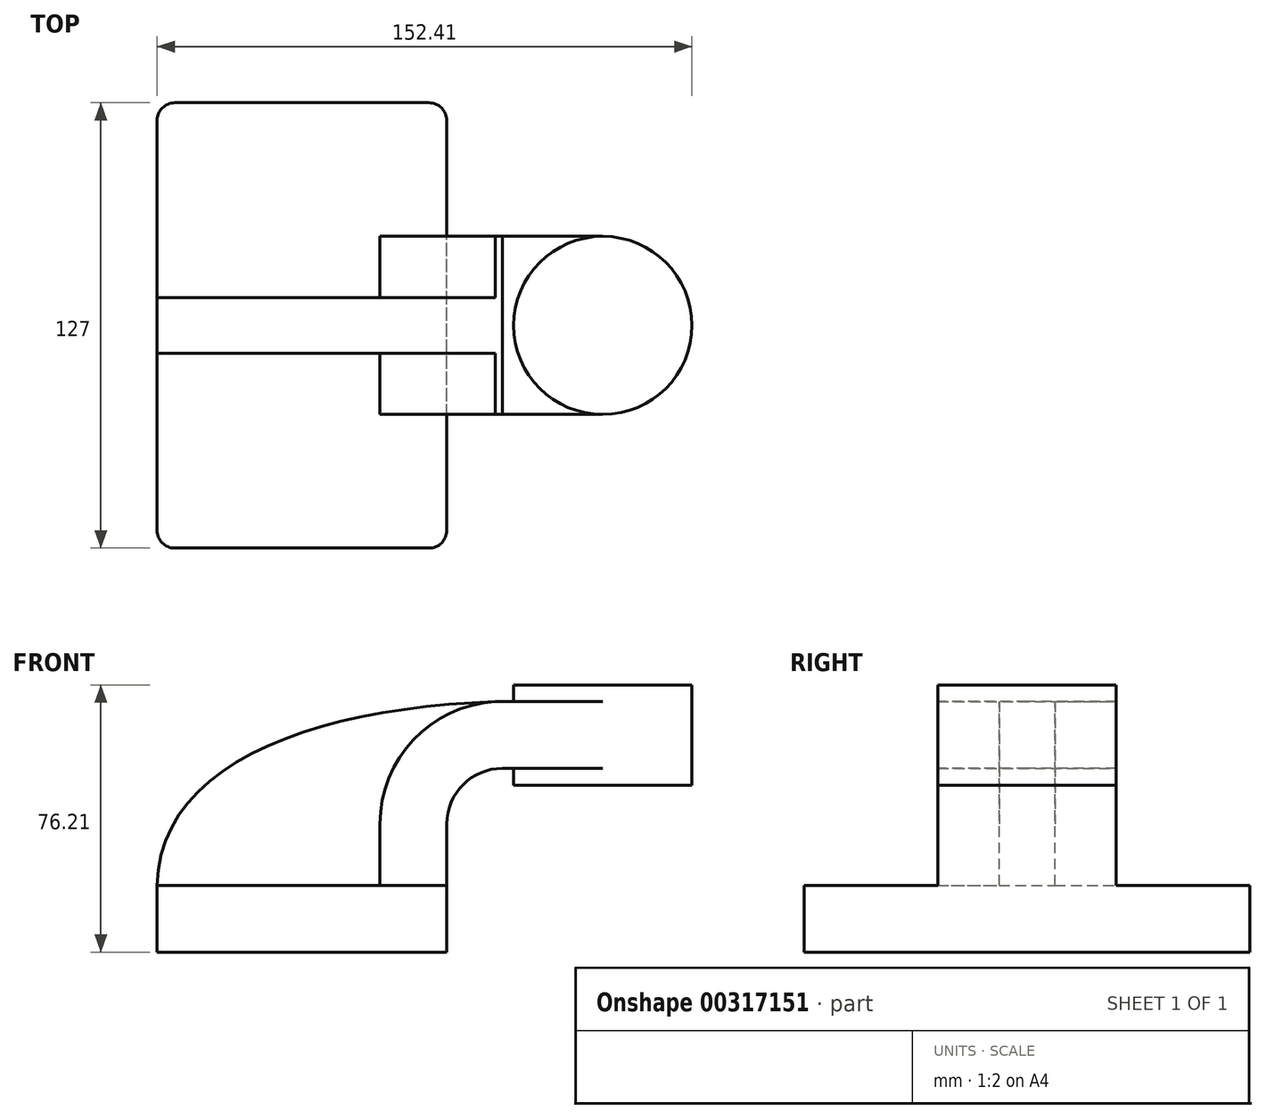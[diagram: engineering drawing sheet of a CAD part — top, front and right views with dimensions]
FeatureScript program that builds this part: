
annotation { "Feature Type Name" : "Feature", "Feature Type Description" : "" }
export const myFeature = defineFeature(function(context is Context, id is Id, definition is map)
    precondition{}
    {
        {
            var Q0;
            Q0=qCreatedBy(makeId("Front.planeOp"),FACE);
            var sketch = newSketch(context, id + "F0", { "sketchPlane" : qUnion([Q0])});
            skLineSegment(sketch, "E0.bottom", {"start": v(-41.28, -9.53) * mm, "end": v(41.28, -9.53) * mm});
            skLineSegment(sketch, "E0.top", {"start": v(-41.28, 9.52) * mm, "end": v(41.28, 9.52) * mm});
            skLineSegment(sketch, "E0.left", {"start": v(-41.28, -9.53) * mm, "end": v(-41.28, 9.52) * mm});
            skLineSegment(sketch, "E0.right", {"start": v(41.28, -9.53) * mm, "end": v(41.28, 9.52) * mm});
            skPoint(sketch, "E0.middle", {"position": v(0, 0) * mm});
            skLineSegment(sketch, "E1.bottom", {"start": v(60.33, 66.68) * mm, "end": v(111.12, 66.68) * mm});
            skLineSegment(sketch, "E1.top", {"start": v(60.33, 38.1) * mm, "end": v(111.12, 38.1) * mm});
            skLineSegment(sketch, "E1.left", {"start": v(60.33, 66.68) * mm, "end": v(60.33, 38.1) * mm});
            skLineSegment(sketch, "E1.right", {"start": v(111.12, 66.68) * mm, "end": v(111.12, 38.1) * mm});
            skPoint(sketch, "E1.middle", {"position": v(85.72, 52.39) * mm});
            skLineSegment(sketch, "E2", {"start": v(41.27, 9.52) * mm, "end": v(41.27, 27) * mm});
            skArc(sketch, "E3", {"start": v(41.27, 27) * mm, "mid": v(45.92, 38.23) * mm, "end": v(57.15, 42.88) * mm});
            skLineSegment(sketch, "E4", {"start": v(57.15, 42.88) * mm, "end": v(85.73, 42.88) * mm});
            skLineSegment(sketch, "E5.0", {"start": v(57.15, 61.93) * mm, "end": v(85.72, 61.93) * mm});
            skArc(sketch, "E5.1", {"start": v(22.22, 27) * mm, "mid": v(32.45, 51.7) * mm, "end": v(57.15, 61.93) * mm});
            skLineSegment(sketch, "E5.2", {"start": v(22.22, 9.52) * mm, "end": v(22.22, 27) * mm});
            skLineSegment(sketch, "E6", {"start": v(85.72, 38.1) * mm, "end": v(85.72, 66.68) * mm});
            skFitSpline(sketch, "E7", {"points": [v(-41.28, 9.53) * mm, v(57.15, 61.93) * mm], "startDerivative": vector(2, 105.97) * mm, "endDerivative": vector(156.9, 3.96) * mm});
            skSolve(sketch);
        }
        {
            var Q0;
            Q0=makeQuery(id+"F0.imprint","IMPRINT",FACE,{"disambiguationData":[TD([[makeQuery(id+"F0.imprint","IMPRINT",EDGE,{"derivedFrom":sQuery(id+"F0.wireOp",EDGE,"E0.bottom")}),1.0]])]});
            extrude(context, id + "F1", {"entities" : qUnion([Q0]), "endBound" : BoundingType.SYMMETRIC, "depth" : 127 * mm});
        }
        {
            var Q0;
            {var subQ1=sQuery(id+"F0.wireOp",EDGE,"E2");Q0=makeQuery(id+"F0.imprint","IMPRINT",FACE,{"disambiguationData":[TD([[makeQuery(id+"F0.imprint","IMPRINT",EDGE,{"derivedFrom":subQ1}),1.0]])]});}
            var Q1;
            {var subQ0=sQuery(id+"F0.wireOp",EDGE,"E5.0");var subQ1=sQuery(id+"F0.wireOp",EDGE,"E1.left");var subQ2=makeQuery(id+"F0.imprint","INTERSECT",VERTEX,{"derivedFrom":[subQ1,subQ0]});Q1=makeQuery(id+"F0.imprint","IMPRINT",FACE,{"disambiguationData":[TD([[makeQuery(id+"F0.imprint","IMPRINT",EDGE,{"disambiguationData":[TD([[subQ2,-1.0]])],"derivedFrom":subQ1}),1.0]])]});}
            extrude(context, id + "F2", {"entities" : qUnion([Q0, Q1]), "operationType" : NewBodyOperationType.ADD, "endBound" : BoundingType.SYMMETRIC, "depth" : 50.8 * mm});
        }
        {
            var Q0;
            {var subQ3=sQuery(id+"F0.wireOp",EDGE,"E5.2");Q0=makeQuery(id+"F0.imprint","IMPRINT",FACE,{"disambiguationData":[TD([[makeQuery(id+"F0.imprint","IMPRINT",EDGE,{"derivedFrom":subQ3}),1.0]])]});}
            var Q1;
            Q1=sQuery(id+"F0.wireOp",EDGE,"E7");
            extrude(context, id + "F3", {"entities" : qUnion([Q0]), "operationType" : NewBodyOperationType.ADD, "surfaceEntities" : qUnion([Q1]), "endBound" : BoundingType.SYMMETRIC, "depth" : 15.88 * mm});
        }
        {
            var Q0;
            {var subQ4=sQuery(id+"F0.wireOp",EDGE,"E1.right");Q0=makeQuery(id+"F0.imprint","IMPRINT",FACE,{"disambiguationData":[TD([[makeQuery(id+"F0.imprint","IMPRINT",EDGE,{"derivedFrom":subQ4}),-1.0]])]});}
            var Q1;
            Q1=sQuery(id+"F0.wireOp",EDGE,"E6");
            revolve(context, id + "F4", {"operationType" : NewBodyOperationType.ADD, "entities" : qUnion([Q0]), "axis" : qUnion([Q1]), "revolveType" : RevolveType.FULL});
        }
        {
            var Q0;
            Q0=makeQuery(id+"F1.opExtrude","CAP_EDGE",EDGE,{"disambiguationData":[OSD([sQuery(id+"F0.wireOp",EDGE,"E0.right")])],"isStart":false});
            var Q1;
            Q1=makeQuery(id+"F1.opExtrude","CAP_EDGE",EDGE,{"disambiguationData":[OSD([sQuery(id+"F0.wireOp",EDGE,"E0.left")])],"isStart":false});
            var Q2;
            Q2=makeQuery(id+"F1.opExtrude","CAP_EDGE",EDGE,{"disambiguationData":[OSD([sQuery(id+"F0.wireOp",EDGE,"E0.right")])],"isStart":true});
            var Q3;
            Q3=makeQuery(id+"F1.opExtrude","CAP_EDGE",EDGE,{"disambiguationData":[OSD([sQuery(id+"F0.wireOp",EDGE,"E0.left")])],"isStart":true});
            fillet(context, id + "F5", {"entities" : qUnion([Q0, Q1, Q2, Q3]), "radius" : 5.08 * mm, "tangentPropagation" : true, "allowEdgeOverflow" : false});
        }
    });
